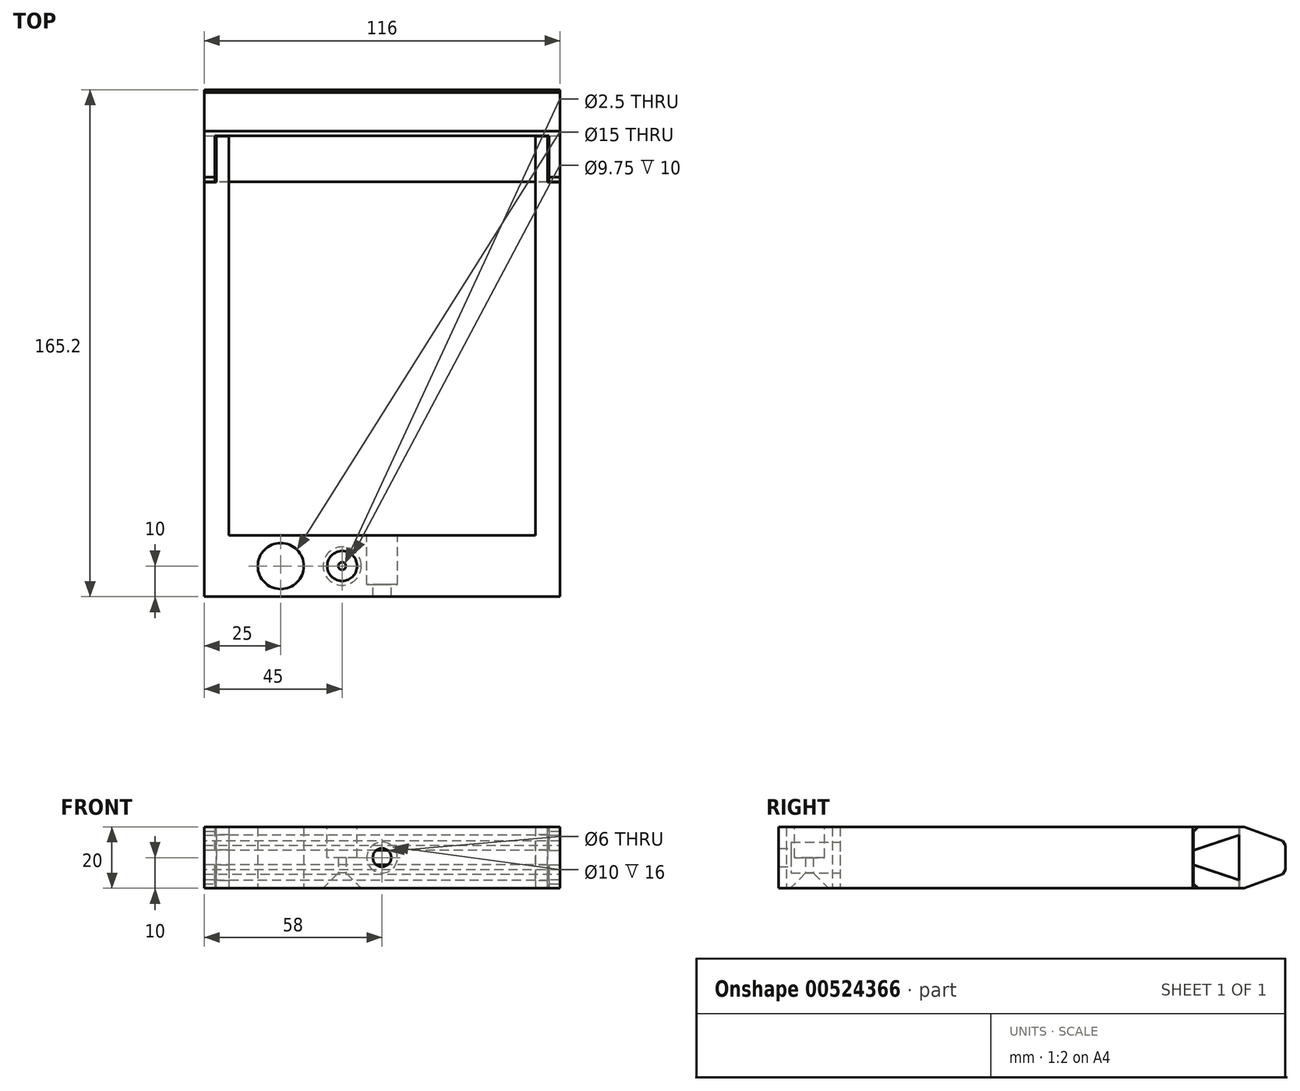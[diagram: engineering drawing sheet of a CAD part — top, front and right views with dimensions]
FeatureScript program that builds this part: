
annotation { "Feature Type Name" : "Feature", "Feature Type Description" : "" }
export const myFeature = defineFeature(function(context is Context, id is Id, definition is map)
    precondition{}
    {
        {
            var Q0;
            Q0=qCreatedBy(makeId("Top.planeOp"),FACE);
            var sketch = newSketch(context, id + "F0", { "sketchPlane" : qUnion([Q0])});
            skLineSegment(sketch, "E0", {"start": v(0, 0) * mm, "end": v(0, 150) * mm});
            skLineSegment(sketch, "E1", {"start": v(0, 150) * mm, "end": v(8, 150) * mm});
            skLineSegment(sketch, "E2", {"start": v(8, 150) * mm, "end": v(8, 20) * mm});
            skLineSegment(sketch, "E3", {"start": v(8, 20) * mm, "end": v(108, 20) * mm});
            skLineSegment(sketch, "E4", {"start": v(108, 20) * mm, "end": v(108, 150) * mm});
            skLineSegment(sketch, "E5", {"start": v(108, 150) * mm, "end": v(116, 150) * mm});
            skLineSegment(sketch, "E6", {"start": v(116, 150) * mm, "end": v(116, 0) * mm});
            skLineSegment(sketch, "E7", {"start": v(116, 0) * mm, "end": v(0, 0) * mm});
            skCircle(sketch, "E8", {"center": v(45, 10) * mm, "radius": 1.25 * mm});
            skPoint(sketch, "E8.centerSnap0", {"position": v(58, 20) * mm});
            skCircle(sketch, "E9", {"center": v(25, 10) * mm, "radius": 7.5 * mm});
            skSolve(sketch);
        }
        {
            var Q0;
            Q0 = qSketchRegion(id + "F0", true);
            extrude(context, id + "F1", {"entities" : qUnion([Q0]), "depth" : 20 * mm, "offsetDistance" : 25 * mm});
        }
        {
            var Q0;
            Q0=makeQuery(id+"F1.opExtrude","SWEPT_FACE",FACE,{"disambiguationData":[OSD([sQuery(id+"F0.wireOp",EDGE,"E0")])]});
            var sketch = newSketch(context, id + "F2", { "sketchPlane" : qUnion([Q0])});
            skLineSegment(sketch, "E10", {"start": v(-150, 2.5) * mm, "end": v(-135, 7.5) * mm});
            skLineSegment(sketch, "E11", {"start": v(-135, 7.5) * mm, "end": v(-135, 12.5) * mm});
            skLineSegment(sketch, "E12", {"start": v(-135, 12.5) * mm, "end": v(-150, 17.5) * mm});
            skLineSegment(sketch, "E13", {"start": v(-150, 17.5) * mm, "end": v(-150, 2.5) * mm});
            skSolve(sketch);
        }
        {
            var Q0;
            Q0 = qSketchRegion(id + "F2", true);
            extrude(context, id + "F3", {"entities" : qUnion([Q0]), "operationType" : NewBodyOperationType.REMOVE, "endBound" : BoundingType.THROUGH_ALL, "oppositeDirection" : true, "depth" : 25 * mm, "offsetDistance" : 25 * mm});
        }
        {
            var Q0;
            Q0=makeQuery(id+"F1.opExtrude","SWEPT_FACE",FACE,{"disambiguationData":[OSD([sQuery(id+"F0.wireOp",EDGE,"E0")])]});
            var sketch = newSketch(context, id + "F4", { "sketchPlane" : qUnion([Q0])});
            skLineSegment(sketch, "E14.0", {"start": v(-150.2, 2.64) * mm, "end": v(-150.2, 0) * mm});
            skLineSegment(sketch, "E14.1", {"start": v(-150.2, 20) * mm, "end": v(-150.2, 17.36) * mm});
            skLineSegment(sketch, "E14.2", {"start": v(-135.2, 12.36) * mm, "end": v(-150.2, 17.36) * mm});
            skLineSegment(sketch, "E14.3", {"start": v(-135.2, 7.64) * mm, "end": v(-135.2, 12.36) * mm});
            skLineSegment(sketch, "E14.4", {"start": v(-150.2, 2.64) * mm, "end": v(-135.2, 7.64) * mm});
            skLineSegment(sketch, "E15", {"start": v(-150.2, 0) * mm, "end": v(-151.7, 0) * mm});
            skLineSegment(sketch, "E16", {"start": v(-151.7, 0) * mm, "end": v(-165.2, 5) * mm});
            skLineSegment(sketch, "E17", {"start": v(-165.2, 5) * mm, "end": v(-165.2, 15) * mm});
            skLineSegment(sketch, "E18", {"start": v(-165.2, 15) * mm, "end": v(-151.7, 20) * mm});
            skLineSegment(sketch, "E19", {"start": v(-151.7, 20) * mm, "end": v(-150.2, 20) * mm});
            skSolve(sketch);
        }
        {
            var Q0;
            Q0 = qSketchRegion(id + "F4", true);
            extrude(context, id + "F5", {"entities" : qUnion([Q0]), "oppositeDirection" : true, "depth" : 116 * mm, "offsetDistance" : 25 * mm});
        }
        {
            var Q0;
            Q0=makeQuery(id+"F1.opExtrude","CAP_FACE",FACE,{"disambiguationData":[OSD([sQuery(id+"F0.wireOp",EDGE,"E0"),sQuery(id+"F0.wireOp",EDGE,"E1"),sQuery(id+"F0.wireOp",EDGE,"E2"),sQuery(id+"F0.wireOp",EDGE,"E3"),sQuery(id+"F0.wireOp",EDGE,"E4"),sQuery(id+"F0.wireOp",EDGE,"E5"),sQuery(id+"F0.wireOp",EDGE,"E6"),sQuery(id+"F0.wireOp",EDGE,"E7"),sQuery(id+"F0.wireOp",EDGE,"E8"),sQuery(id+"F0.wireOp",EDGE,"E9")])],"isStart":false});
            var sketch = newSketch(context, id + "F6", { "sketchPlane" : qUnion([Q0])});
            skLineSegment(sketch, "E20.bottom", {"start": v(0, 150) * mm, "end": v(4, 150) * mm});
            skLineSegment(sketch, "E20.top", {"start": v(0, 135) * mm, "end": v(4, 135) * mm});
            skLineSegment(sketch, "E20.left", {"start": v(0, 150) * mm, "end": v(0, 135) * mm});
            skLineSegment(sketch, "E20.right", {"start": v(4, 150) * mm, "end": v(4, 135) * mm});
            skLineSegment(sketch, "E21.bottom", {"start": v(116, 150) * mm, "end": v(112, 150) * mm});
            skLineSegment(sketch, "E21.top", {"start": v(116, 135) * mm, "end": v(112, 135) * mm});
            skLineSegment(sketch, "E21.left", {"start": v(116, 150) * mm, "end": v(116, 135) * mm});
            skLineSegment(sketch, "E21.right", {"start": v(112, 150) * mm, "end": v(112, 135) * mm});
            skSolve(sketch);
        }
        {
            var Q0;
            Q0 = qSketchRegion(id + "F6", true);
            extrude(context, id + "F7", {"entities" : qUnion([Q0]), "operationType" : NewBodyOperationType.REMOVE, "endBound" : BoundingType.THROUGH_ALL, "oppositeDirection" : true, "depth" : 25 * mm, "offsetDistance" : 25 * mm});
        }
        {
            var Q0;
            Q0=makeQuery(id+"F5.opExtrude","CAP_FACE",FACE,{"disambiguationData":[OSD([sQuery(id+"F4.wireOp",EDGE,"E14.0"),sQuery(id+"F4.wireOp",EDGE,"E14.1"),sQuery(id+"F4.wireOp",EDGE,"E14.2"),sQuery(id+"F4.wireOp",EDGE,"E14.3"),sQuery(id+"F4.wireOp",EDGE,"E14.4"),sQuery(id+"F4.wireOp",EDGE,"E15"),sQuery(id+"F4.wireOp",EDGE,"E16"),sQuery(id+"F4.wireOp",EDGE,"E17"),sQuery(id+"F4.wireOp",EDGE,"E18"),sQuery(id+"F4.wireOp",EDGE,"E19")])],"isStart":true});
            var sketch = newSketch(context, id + "F8", { "sketchPlane" : qUnion([Q0])});
            skLineSegment(sketch, "E22.0", {"start": v(-150.2, 20) * mm, "end": v(-150.2, 17.36) * mm});
            skLineSegment(sketch, "E23.0", {"start": v(-135.2, 12.36) * mm, "end": v(-150.2, 17.36) * mm});
            skLineSegment(sketch, "E24.0", {"start": v(-150.2, 2.64) * mm, "end": v(-135.2, 7.64) * mm});
            skLineSegment(sketch, "E25.0", {"start": v(-150.2, 2.64) * mm, "end": v(-150.2, 0) * mm});
            skLineSegment(sketch, "E26", {"start": v(-135.2, 12.36) * mm, "end": v(-135.2, 20) * mm});
            skLineSegment(sketch, "E27", {"start": v(-135.2, 20) * mm, "end": v(-150.2, 20) * mm});
            skLineSegment(sketch, "E28", {"start": v(-150.2, 0) * mm, "end": v(-135.2, 0) * mm});
            skLineSegment(sketch, "E29", {"start": v(-135.2, 0) * mm, "end": v(-135.2, 7.64) * mm});
            skSolve(sketch);
        }
        {
            var Q0;
            Q0 = qSketchRegion(id + "F8", true);
            extrude(context, id + "F9", {"entities" : qUnion([Q0]), "operationType" : NewBodyOperationType.ADD, "oppositeDirection" : true, "depth" : 3.5 * mm, "offsetDistance" : 25 * mm});
        }
        {
            var Q0;
            Q0=makeQuery(id+"F5.opExtrude","CAP_FACE",FACE,{"disambiguationData":[OSD([sQuery(id+"F4.wireOp",EDGE,"E14.0"),sQuery(id+"F4.wireOp",EDGE,"E14.1"),sQuery(id+"F4.wireOp",EDGE,"E14.2"),sQuery(id+"F4.wireOp",EDGE,"E14.3"),sQuery(id+"F4.wireOp",EDGE,"E14.4"),sQuery(id+"F4.wireOp",EDGE,"E15"),sQuery(id+"F4.wireOp",EDGE,"E16"),sQuery(id+"F4.wireOp",EDGE,"E17"),sQuery(id+"F4.wireOp",EDGE,"E18"),sQuery(id+"F4.wireOp",EDGE,"E19")])],"isStart":false});
            var sketch = newSketch(context, id + "F10", { "sketchPlane" : qUnion([Q0])});
            skLineSegment(sketch, "E30.0.0", {"start": v(135.2, 20) * mm, "end": v(135.2, 12.36) * mm});
            skLineSegment(sketch, "E30.0.1", {"start": v(135.2, 12.36) * mm, "end": v(150.2, 17.36) * mm});
            skLineSegment(sketch, "E30.0.2", {"start": v(150.2, 17.36) * mm, "end": v(150.2, 20) * mm});
            skLineSegment(sketch, "E30.0.3", {"start": v(150.2, 20) * mm, "end": v(135.2, 20) * mm});
            skLineSegment(sketch, "E31.0.0", {"start": v(135.2, 0) * mm, "end": v(150.2, 0) * mm});
            skLineSegment(sketch, "E31.0.1", {"start": v(150.2, 0) * mm, "end": v(150.2, 2.64) * mm});
            skLineSegment(sketch, "E31.0.2", {"start": v(150.2, 2.64) * mm, "end": v(135.2, 7.64) * mm});
            skLineSegment(sketch, "E31.0.3", {"start": v(135.2, 7.64) * mm, "end": v(135.2, 0) * mm});
            skSolve(sketch);
        }
        {
            var Q0;
            Q0 = qSketchRegion(id + "F10", true);
            extrude(context, id + "F11", {"entities" : qUnion([Q0]), "operationType" : NewBodyOperationType.ADD, "oppositeDirection" : true, "depth" : 3.5 * mm, "offsetDistance" : 25 * mm});
        }
        {
            var Q0;
            Q0=makeQuery(id+"F5.opExtrude","SWEPT_EDGE",EDGE,{"disambiguationData":[OSD([sQuery(id+"F4.wireOp",EDGE,"E16"),sQuery(id+"F4.wireOp",EDGE,"E17")])]});
            var Q1;
            Q1=makeQuery(id+"F5.opExtrude","SWEPT_EDGE",EDGE,{"disambiguationData":[OSD([sQuery(id+"F4.wireOp",EDGE,"E17"),sQuery(id+"F4.wireOp",EDGE,"E18")])]});
            var Q2;
            Q2=makeQuery(id+"F9.opExtrude","SWEPT_EDGE",EDGE,{"disambiguationData":[OSD([sQuery(id+"F8.wireOp",EDGE,"E28"),sQuery(id+"F8.wireOp",EDGE,"E29")])]});
            var Q3;
            Q3=makeQuery(id+"F9.opExtrude","SWEPT_EDGE",EDGE,{"disambiguationData":[OSD([sQuery(id+"F8.wireOp",EDGE,"E26"),sQuery(id+"F8.wireOp",EDGE,"E27")])]});
            var Q4;
            Q4=makeQuery(id+"F11.opExtrude","SWEPT_EDGE",EDGE,{"disambiguationData":[OSD([sQuery(id+"F10.wireOp",EDGE,"E31.0.0"),sQuery(id+"F10.wireOp",EDGE,"E31.0.3")])]});
            var Q5;
            Q5=makeQuery(id+"F11.opExtrude","SWEPT_EDGE",EDGE,{"disambiguationData":[OSD([sQuery(id+"F10.wireOp",EDGE,"E30.0.0"),sQuery(id+"F10.wireOp",EDGE,"E30.0.3")])]});
            chamfer(context, id + "F12", {"entities" : qUnion([Q0, Q1, Q2, Q3, Q4, Q5]), "width" : 1.5 * mm, "tangentPropagation" : true});
        }
        {
            var Q0;
            Q0=makeQuery(id+"F1.opExtrude","SWEPT_FACE",FACE,{"disambiguationData":[OSD([sQuery(id+"F0.wireOp",EDGE,"E3")])]});
            var sketch = newSketch(context, id + "F13", { "sketchPlane" : qUnion([Q0])});
            skCircle(sketch, "E32", {"center": v(-58, 10) * mm, "radius": 3 * mm});
            skPoint(sketch, "E32.centerSnap0", {"position": v(-58, 0) * mm});
            skPoint(sketch, "E32.centerSnap1", {"position": v(-8, 10) * mm});
            skSolve(sketch);
        }
        {
            var Q0;
            Q0 = qSketchRegion(id + "F13", true);
            extrude(context, id + "F14", {"entities" : qUnion([Q0]), "operationType" : NewBodyOperationType.REMOVE, "endBound" : BoundingType.THROUGH_ALL, "oppositeDirection" : true, "depth" : 25 * mm, "offsetDistance" : 25 * mm});
        }
        {
            var Q0;
            Q0=makeQuery(id+"F1.opExtrude","SWEPT_FACE",FACE,{"disambiguationData":[OSD([sQuery(id+"F0.wireOp",EDGE,"E3")])]});
            var sketch = newSketch(context, id + "F15", { "sketchPlane" : qUnion([Q0])});
            skCircle(sketch, "E33", {"center": v(-58, 10) * mm, "radius": 5 * mm});
            skSolve(sketch);
        }
        {
            var Q0;
            Q0 = qSketchRegion(id + "F15", true);
            extrude(context, id + "F16", {"entities" : qUnion([Q0]), "operationType" : NewBodyOperationType.REMOVE, "oppositeDirection" : true, "depth" : 16 * mm, "offsetDistance" : 25 * mm});
        }
        {
            var Q0;
            Q0=makeQuery(id+"F1.opExtrude","CAP_FACE",FACE,{"disambiguationData":[OSD([sQuery(id+"F0.wireOp",EDGE,"E0"),sQuery(id+"F0.wireOp",EDGE,"E1"),sQuery(id+"F0.wireOp",EDGE,"E2"),sQuery(id+"F0.wireOp",EDGE,"E3"),sQuery(id+"F0.wireOp",EDGE,"E4"),sQuery(id+"F0.wireOp",EDGE,"E5"),sQuery(id+"F0.wireOp",EDGE,"E6"),sQuery(id+"F0.wireOp",EDGE,"E7"),sQuery(id+"F0.wireOp",EDGE,"E8"),sQuery(id+"F0.wireOp",EDGE,"E9")])],"isStart":false});
            var sketch = newSketch(context, id + "F17", { "sketchPlane" : qUnion([Q0])});
            skCircle(sketch, "E34", {"center": v(45, 10) * mm, "radius": 4.88 * mm});
            skSolve(sketch);
        }
        {
            var Q0;
            Q0 = qSketchRegion(id + "F17", true);
            extrude(context, id + "F18", {"entities" : qUnion([Q0]), "operationType" : NewBodyOperationType.REMOVE, "oppositeDirection" : true, "depth" : 10 * mm, "offsetDistance" : 25 * mm});
        }
        {
            var Q0;
            Q0=makeQuery(id+"F1.opExtrude","CAP_EDGE",EDGE,{"disambiguationData":[OSD([sQuery(id+"F0.wireOp",EDGE,"E8")])],"isStart":true});
            chamfer(context, id + "F19", {"entities" : qUnion([Q0]), "width" : 5 * mm, "tangentPropagation" : true});
        }
    });
